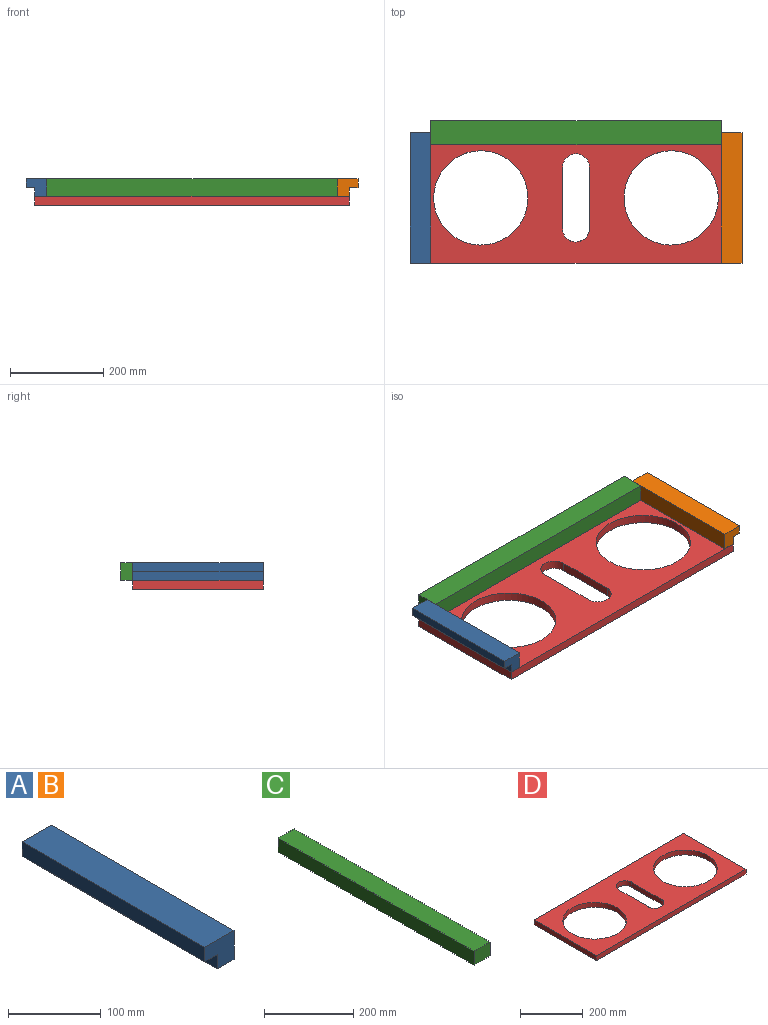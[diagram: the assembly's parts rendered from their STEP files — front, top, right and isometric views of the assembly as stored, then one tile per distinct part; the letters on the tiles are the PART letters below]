
ASSEMBLY  parts=4 mates=3
PART A: 8 faces, bbox 44.5x279.4x38.1 mm
  f0: plane 279.4x19.05mm, normal (-1,0,0), area 5322.6mm2, adj f1,f5,f6,f7
  f1: plane 279.4x19.05mm, normal (0,0,-1), area 5322.6mm2, adj f0,f2,f6,f7
  f2: plane 279.4x19.05mm, normal (-1,0,0), area 5322.6mm2, adj f1,f3,f6,f7
  f3: plane 279.4x25.4mm, normal (0,0,-1), area 7096.8mm2, adj f2,f4,f6,f7
  f4: plane 279.4x38.1mm, normal (1,0,0), area 10645.1mm2, adj f3,f5,f6,f7
  f5: plane 279.4x44.45mm, normal (0,0,1), area 12419.3mm2, adj f0,f4,f6,f7
  f6: plane 44.45x38.1mm, normal (0,-1,0), area 1330.6mm2, adj f0,f1,f2,f3,f4,f5
  f7: plane 44.45x38.1mm, normal (0,1,0), area 1330.6mm2, adj f0,f1,f2,f3,f4,f5
PART B: same geometry as A
PART C: 6 faces, bbox 50.8x622.3x38.1 mm
  f0: plane 622.3x38.1mm, normal (-1,0,0), area 23709.6mm2, adj f1,f3,f4,f5
  f1: plane 622.3x50.8mm, normal (0,0,-1), area 31612.8mm2, adj f0,f2,f4,f5
  f2: plane 622.3x38.1mm, normal (1,0,0), area 23709.6mm2, adj f1,f3,f4,f5
  f3: plane 622.3x50.8mm, normal (0,0,1), area 31612.8mm2, adj f0,f2,f4,f5
  f4: plane 50.8x38.1mm, normal (0,-1,0), area 1935.5mm2, adj f0,f1,f2,f3
  f5: plane 50.8x38.1mm, normal (0,1,0), area 1935.5mm2, adj f0,f1,f2,f3
PART D: 12 faces, bbox 673.1x279.4x19.1 mm
  f0: plane 673.1x19.05mm, normal (0,-1,0), area 12822.6mm2, adj f1,f9,f10,f11
  f1: plane 279.4x19.05mm, normal (1,0,0), area 5322.6mm2, adj f0,f2,f10,f11
  f2: plane 673.1x19.05mm, normal (0,1,0), area 12822.6mm2, adj f1,f9,f10,f11
  f3: plane 131x19.05mm, normal (1,0,0), area 2495.6mm2, adj f4,f8,f10,f11
  f4: cylinder r=29mm len=58mm, axis (0,0,-1), area 1735.6mm2, adj f3,f5,f10,f11
  f5: plane 131x19.05mm, normal (-1,0,0), area 2495.6mm2, adj f4,f8,f10,f11
  f6: cylinder r=100.97mm len=201.93mm, axis (0,0,-1), area 12085mm2, adj f10,f11
  f7: cylinder r=100.97mm len=201.93mm, axis (0,0,-1), area 12085mm2, adj f10,f11
  f8: extruded ~58x29mm, area 1735.6mm2, adj f3,f5,f10,f11
  f9: plane 279.4x19.05mm, normal (-1,0,0), area 5322.6mm2, adj f0,f2,f10,f11
  f10: plane 673.1x279.4mm, normal (0,0,1), area 113773.5mm2, adj f0,f1,f2,f3,f4,f5,f6,f7
  f11: plane 673.1x279.4mm, normal (0,0,-1), area 113773.5mm2, adj f0,f1,f2,f3,f4,f5,f6,f7
PLACE A t=(-355.6,173.23,19.05)mm
PLACE B rot(axis=(0,0,-1),180deg) t=(355.6,-106.17,19.05)mm
PLACE C rot(axis=(0,0,1),90deg) t=(-311.15,147.83,19.05)mm
PLACE D t=(0,33.53,0)mm
MATE fastened C.f1 <-> D.f10  axis (0,0,-1) through (0,198.63,19.05)mm
MATE fastened B.f7 <-> D.f0  axis (0,-1,0) through (336.55,-106.17,19.05)mm
MATE fastened A.f6 <-> D.f0  axis (0,-1,0) through (-336.55,-106.17,19.05)mm
